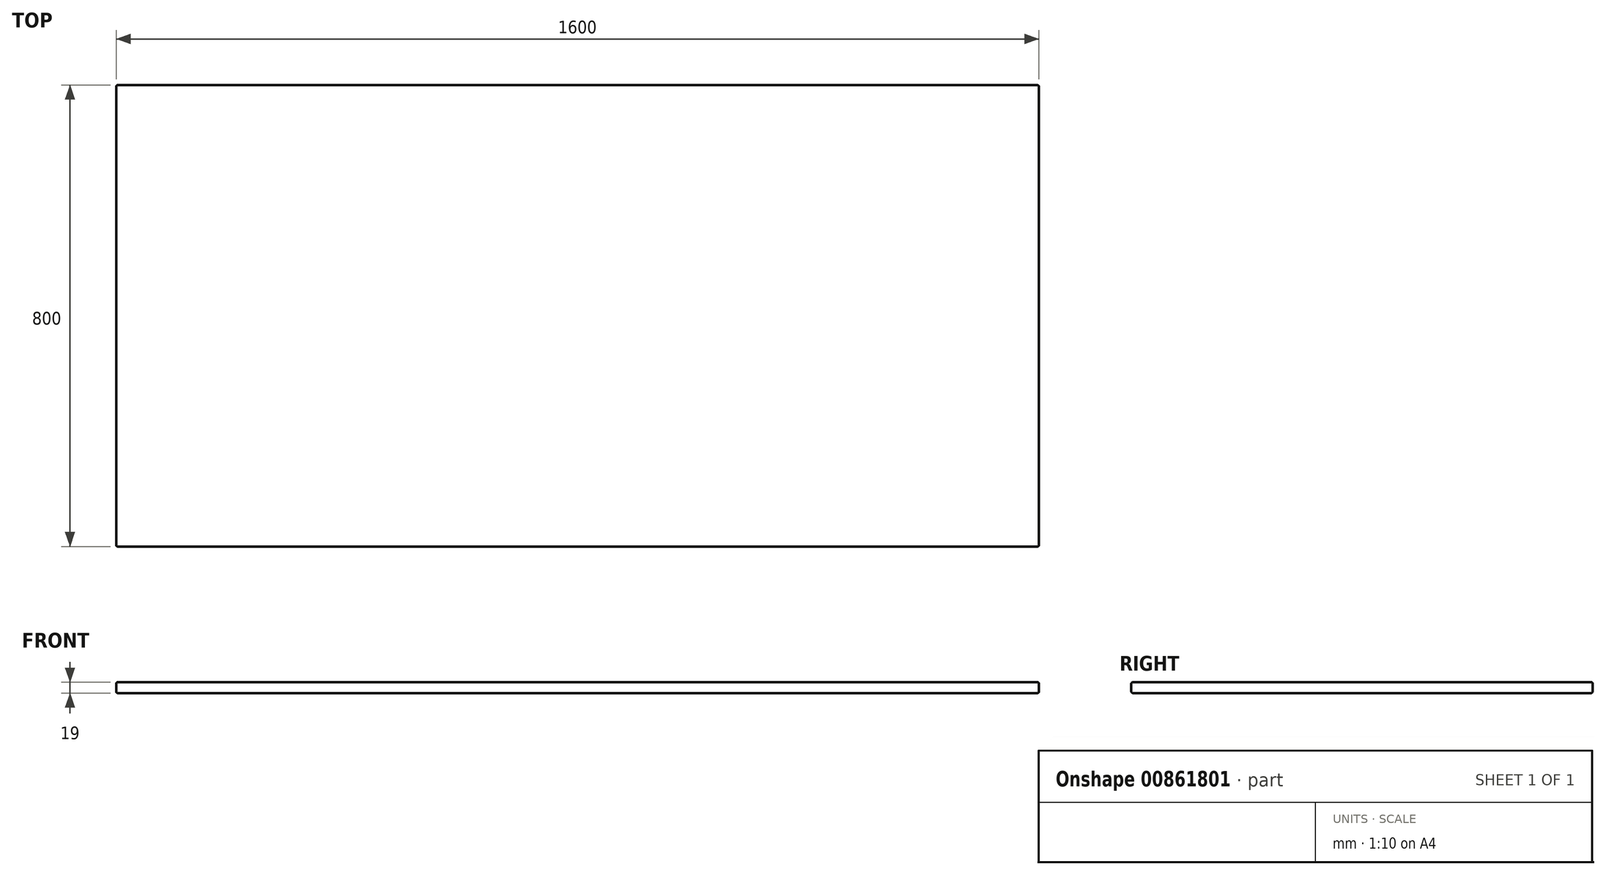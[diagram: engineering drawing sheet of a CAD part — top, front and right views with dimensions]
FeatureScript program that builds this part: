
annotation { "Feature Type Name" : "Feature", "Feature Type Description" : "" }
export const myFeature = defineFeature(function(context is Context, id is Id, definition is map)
    precondition{}
    {
        {
            var Q0;
            Q0=qCreatedBy(makeId("Top.planeOp"),FACE);
            var sketch = newSketch(context, id + "F0", { "sketchPlane" : qUnion([Q0])});
            skLineSegment(sketch, "E0.bottom", {"start": v(-800, 400) * mm, "end": v(800, 400) * mm});
            skLineSegment(sketch, "E0.top", {"start": v(-800, -400) * mm, "end": v(800, -400) * mm});
            skLineSegment(sketch, "E0.left", {"start": v(-800, 400) * mm, "end": v(-800, -400) * mm});
            skLineSegment(sketch, "E0.right", {"start": v(800, 400) * mm, "end": v(800, -400) * mm});
            skLineSegment(sketch, "E1", {"start": v(-800, -400) * mm, "end": v(800, 400) * mm, "construction": true});
            skLineSegment(sketch, "E2", {"start": v(-800, 400) * mm, "end": v(800, -400) * mm, "construction": true});
            skSolve(sketch);
        }
        {
            var Q0;
            Q0 = qSketchRegion(id + "F0", true);
            extrude(context, id + "F1", {"entities" : qUnion([Q0]), "depth" : 19 * mm, "offsetDistance" : 25 * mm});
        }
        {
            var Q0;
            Q0=makeQuery(id+"F1.opExtrude","CAP_EDGE",EDGE,{"disambiguationData":[OSD([sQuery(id+"F0.wireOp",EDGE,"E0.left")])],"isStart":true});
            var Q1;
            Q1=makeQuery(id+"F1.opExtrude","CAP_EDGE",EDGE,{"disambiguationData":[OSD([sQuery(id+"F0.wireOp",EDGE,"E0.left")])],"isStart":false});
            var Q2;
            Q2=makeQuery(id+"F1.opExtrude","SWEPT_EDGE",EDGE,{"disambiguationData":[OSD([sQuery(id+"F0.wireOp",EDGE,"E0.top"),sQuery(id+"F0.wireOp",EDGE,"E0.left")])]});
            var Q3;
            Q3=makeQuery(id+"F1.opExtrude","CAP_EDGE",EDGE,{"disambiguationData":[OSD([sQuery(id+"F0.wireOp",EDGE,"E0.top")])],"isStart":false});
            var Q4;
            Q4=makeQuery(id+"F1.opExtrude","CAP_EDGE",EDGE,{"disambiguationData":[OSD([sQuery(id+"F0.wireOp",EDGE,"E0.top")])],"isStart":true});
            var Q5;
            Q5=makeQuery(id+"F1.opExtrude","SWEPT_EDGE",EDGE,{"disambiguationData":[OSD([sQuery(id+"F0.wireOp",EDGE,"E0.top"),sQuery(id+"F0.wireOp",EDGE,"E0.right")])]});
            var Q6;
            Q6=makeQuery(id+"F1.opExtrude","CAP_EDGE",EDGE,{"disambiguationData":[OSD([sQuery(id+"F0.wireOp",EDGE,"E0.right")])],"isStart":false});
            var Q7;
            Q7=makeQuery(id+"F1.opExtrude","CAP_EDGE",EDGE,{"disambiguationData":[OSD([sQuery(id+"F0.wireOp",EDGE,"E0.bottom")])],"isStart":false});
            var Q8;
            Q8=makeQuery(id+"F1.opExtrude","CAP_EDGE",EDGE,{"disambiguationData":[OSD([sQuery(id+"F0.wireOp",EDGE,"E0.bottom")])],"isStart":true});
            var Q9;
            Q9=makeQuery(id+"F1.opExtrude","CAP_EDGE",EDGE,{"disambiguationData":[OSD([sQuery(id+"F0.wireOp",EDGE,"E0.right")])],"isStart":true});
            var Q10;
            Q10=makeQuery(id+"F1.opExtrude","SWEPT_EDGE",EDGE,{"disambiguationData":[OSD([sQuery(id+"F0.wireOp",EDGE,"E0.bottom"),sQuery(id+"F0.wireOp",EDGE,"E0.right")])]});
            var Q11;
            Q11=makeQuery(id+"F1.opExtrude","SWEPT_EDGE",EDGE,{"disambiguationData":[OSD([sQuery(id+"F0.wireOp",EDGE,"E0.bottom"),sQuery(id+"F0.wireOp",EDGE,"E0.left")])]});
            fillet(context, id + "F2", {"entities" : qUnion([Q0, Q1, Q2, Q3, Q4, Q5, Q6, Q7, Q8, Q9, Q10, Q11]), "radius" : 3 * mm, "tangentPropagation" : true, "allowEdgeOverflow" : false});
        }
    });
